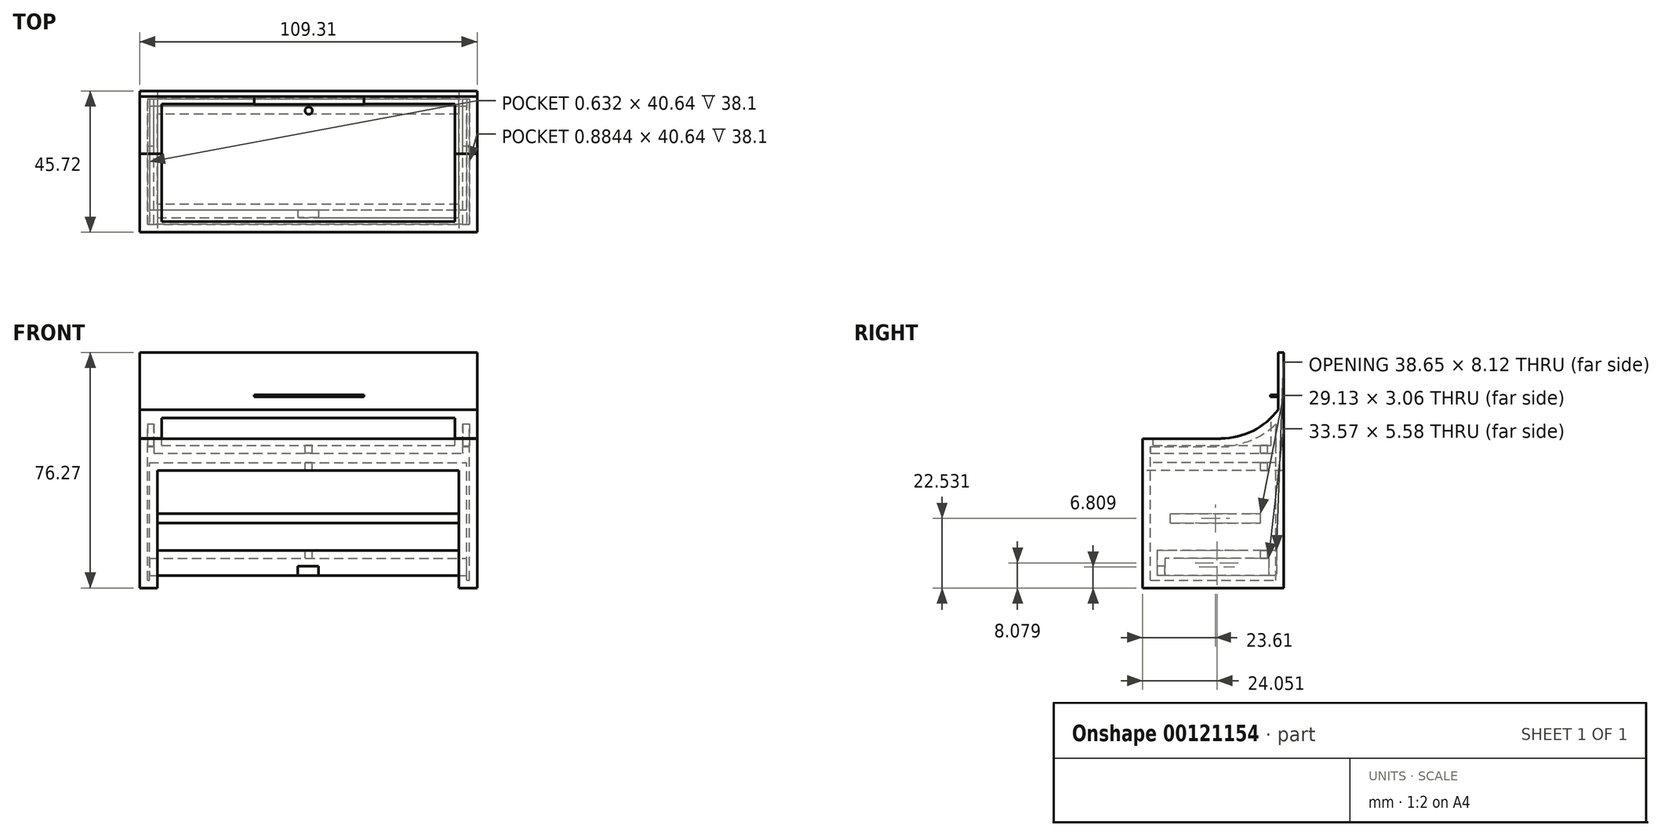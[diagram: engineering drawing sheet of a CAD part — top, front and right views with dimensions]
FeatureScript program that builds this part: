
annotation { "Feature Type Name" : "Feature", "Feature Type Description" : "" }
export const myFeature = defineFeature(function(context is Context, id is Id, definition is map)
    precondition{}
    {
        {
            var Q0;
            Q0=qCreatedBy(makeId("Front.planeOp"),FACE);
            var sketch = newSketch(context, id + "F0", { "sketchPlane" : qUnion([Q0])});
            skLineSegment(sketch, "E0.bottom", {"start": v(-54.76, 0) * mm, "end": v(54.55, 0) * mm});
            skLineSegment(sketch, "E0.top", {"start": v(-54.76, 33.44) * mm, "end": v(54.55, 33.44) * mm});
            skLineSegment(sketch, "E0.left", {"start": v(-54.76, 0) * mm, "end": v(-54.76, 33.44) * mm});
            skLineSegment(sketch, "E0.right", {"start": v(54.55, 0) * mm, "end": v(54.55, 33.44) * mm});
            skSolve(sketch);
        }
        {
            var Q0;
            Q0=makeQuery(id+"F0.imprint","IMPRINT",FACE,{"disambiguationData":[TD([[makeQuery(id+"F0.imprint","IMPRINT",EDGE,{"derivedFrom":sQuery(id+"F0.wireOp",EDGE,"E0.bottom")}),1.0]])]});
            extrude(context, id + "F1", {"entities" : qUnion([Q0]), "depth" : 45.72 * mm});
        }
        {
            var Q0;
            Q0=makeQuery(id+"F1.opExtrude","SWEPT_FACE",FACE,{"disambiguationData":[OSD([sQuery(id+"F0.wireOp",EDGE,"E0.top")])]});
            var sketch = newSketch(context, id + "F2", { "sketchPlane" : qUnion([Q0])});
            skLineSegment(sketch, "E1.bottom", {"start": v(-47.64, -42.28) * mm, "end": v(47.4, -42.28) * mm});
            skLineSegment(sketch, "E1.top", {"start": v(-47.64, -4.14) * mm, "end": v(47.4, -4.14) * mm});
            skLineSegment(sketch, "E1.left", {"start": v(-47.64, -42.28) * mm, "end": v(-47.64, -4.14) * mm});
            skLineSegment(sketch, "E1.right", {"start": v(47.4, -42.28) * mm, "end": v(47.4, -4.14) * mm});
            skSolve(sketch);
        }
        {
            var Q0;
            Q0=makeQuery(id+"F2.imprint","IMPRINT",FACE,{"disambiguationData":[TD([[makeQuery(id+"F2.imprint","IMPRINT",EDGE,{"derivedFrom":sQuery(id+"F2.wireOp",EDGE,"E1.bottom")}),1.0]])]});
            extrude(context, id + "F3", {"entities" : qUnion([Q0]), "operationType" : NewBodyOperationType.REMOVE, "oppositeDirection" : true, "depth" : 25.4 * mm});
        }
        {
            var Q0;
            Q0=makeQuery(id+"F1.opExtrude","CAP_FACE",FACE,{"disambiguationData":[OSD([sQuery(id+"F0.wireOp",EDGE,"E0.bottom"),sQuery(id+"F0.wireOp",EDGE,"E0.top"),sQuery(id+"F0.wireOp",EDGE,"E0.left"),sQuery(id+"F0.wireOp",EDGE,"E0.right")])],"isStart":false});
            var sketch = newSketch(context, id + "F4", { "sketchPlane" : qUnion([Q0])});
            skLineSegment(sketch, "E2.bottom", {"start": v(-54.76, 10.2) * mm, "end": v(54.55, 10.2) * mm});
            skLineSegment(sketch, "E2.top", {"start": v(-54.76, 33.44) * mm, "end": v(54.55, 33.44) * mm});
            skLineSegment(sketch, "E2.left", {"start": v(-54.76, 10.2) * mm, "end": v(-54.76, 33.44) * mm});
            skLineSegment(sketch, "E2.right", {"start": v(54.55, 10.2) * mm, "end": v(54.55, 33.44) * mm});
            skSolve(sketch);
        }
        {
            var Q0;
            Q0=makeQuery(id+"F4.imprint","IMPRINT",FACE,{"disambiguationData":[TD([[makeQuery(id+"F4.imprint","IMPRINT",EDGE,{"derivedFrom":sQuery(id+"F4.wireOp",EDGE,"E2.bottom")}),1.0]])]});
            extrude(context, id + "F5", {"entities" : qUnion([Q0]), "operationType" : NewBodyOperationType.REMOVE, "oppositeDirection" : true, "depth" : 25.4 * mm});
        }
        {
            var Q0;
            Q0=makeQuery(id+"F1.opExtrude","SWEPT_FACE",FACE,{"disambiguationData":[OSD([sQuery(id+"F0.wireOp",EDGE,"E0.right")])]});
            var sketch = newSketch(context, id + "F6", { "sketchPlane" : qUnion([Q0])});
            skCircle(sketch, "E3", {"center": v(-20.32, 33.44) * mm, "radius": 23.08 * mm});
            skSolve(sketch);
        }
        {
            var Q0;
            {var subQ1=sQuery(id+"F0.wireOp",EDGE,"E0.right");var subQ6=makeQuery(id+"F1.opExtrude","SWEPT_EDGE",EDGE,{"disambiguationData":[OSD([sQuery(id+"F0.wireOp",EDGE,"E0.top"),subQ1])]});Q0=makeQuery(id+"F6.imprint","IMPRINT",FACE,{"disambiguationData":[TD([[makeQuery(id+"F6.imprint","IMPRINT",EDGE,{"derivedFrom":subQ6}),1.0]])]});}
            var Q1;
            {var subQ1=sQuery(id+"F0.wireOp",EDGE,"E0.right");var subQ6=makeQuery(id+"F1.opExtrude","SWEPT_EDGE",EDGE,{"disambiguationData":[OSD([sQuery(id+"F0.wireOp",EDGE,"E0.top"),subQ1])]});Q1=makeQuery(id+"F6.imprint","IMPRINT",FACE,{"disambiguationData":[TD([[makeQuery(id+"F6.imprint","IMPRINT",EDGE,{"derivedFrom":subQ6}),-1.0]])]});}
            extrude(context, id + "F7", {"entities" : qUnion([Q0, Q1]), "operationType" : NewBodyOperationType.REMOVE, "oppositeDirection" : true, "depth" : 254 * mm});
        }
        {
            var Q0;
            Q0=makeQuery(id+"F3.boolean.opBoolean","COPY",FACE,{"derivedFrom":makeQuery(id+"F3.opExtrude","CAP_FACE",FACE,{"disambiguationData":[OSD([sQuery(id+"F2.wireOp",EDGE,"E1.bottom"),sQuery(id+"F2.wireOp",EDGE,"E1.top"),sQuery(id+"F2.wireOp",EDGE,"E1.left"),sQuery(id+"F2.wireOp",EDGE,"E1.right")])],"isStart":false})});
            var sketch = newSketch(context, id + "F8", { "sketchPlane" : qUnion([Q0])});
            skCircle(sketch, "E4", {"center": v(0, -6.36) * mm, "radius": 1.17 * mm});
            skSolve(sketch);
        }
        {
            var Q0;
            Q0=makeQuery(id+"F1.opExtrude","SWEPT_FACE",FACE,{"disambiguationData":[OSD([sQuery(id+"F0.wireOp",EDGE,"E0.bottom")])]});
            var sketch = newSketch(context, id + "F9", { "sketchPlane" : qUnion([Q0])});
            skLineSegment(sketch, "E5.bottom", {"start": v(-54.76, 0) * mm, "end": v(-49.05, 0) * mm});
            skLineSegment(sketch, "E5.top", {"start": v(-54.76, 45.72) * mm, "end": v(-49.05, 45.72) * mm});
            skLineSegment(sketch, "E5.left", {"start": v(-54.76, 0) * mm, "end": v(-54.76, 45.72) * mm});
            skLineSegment(sketch, "E5.right", {"start": v(-49.05, 0) * mm, "end": v(-49.05, 45.72) * mm});
            skLineSegment(sketch, "E6.bottom", {"start": v(54.55, 0) * mm, "end": v(48.6, 0) * mm});
            skLineSegment(sketch, "E6.top", {"start": v(54.55, 45.72) * mm, "end": v(48.6, 45.72) * mm});
            skLineSegment(sketch, "E6.left", {"start": v(54.55, 0) * mm, "end": v(54.55, 45.72) * mm});
            skLineSegment(sketch, "E6.right", {"start": v(48.6, 0) * mm, "end": v(48.6, 45.72) * mm});
            skSolve(sketch);
        }
        {
            var Q0;
            Q0=makeQuery(id+"F9.imprint","IMPRINT",FACE,{"disambiguationData":[TD([[makeQuery(id+"F9.imprint","IMPRINT",EDGE,{"derivedFrom":sQuery(id+"F9.wireOp",EDGE,"E6.bottom")}),1.0]])]});
            var Q1;
            Q1=makeQuery(id+"F9.imprint","IMPRINT",FACE,{"disambiguationData":[TD([[makeQuery(id+"F9.imprint","IMPRINT",EDGE,{"derivedFrom":sQuery(id+"F9.wireOp",EDGE,"E5.bottom")}),1.0]])]});
            extrude(context, id + "F10", {"entities" : qUnion([Q0, Q1]), "operationType" : NewBodyOperationType.ADD, "depth" : 38.1 * mm});
        }
        {
            var Q0;
            Q0=makeQuery(id+"F10.opExtrude","SWEPT_FACE",FACE,{"disambiguationData":[OSD([sQuery(id+"F9.wireOp",EDGE,"E5.right")])]});
            var sketch = newSketch(context, id + "F11", { "sketchPlane" : qUnion([Q0])});
            skLineSegment(sketch, "E7.bottom", {"start": v(-36.68, -17.1) * mm, "end": v(-7.55, -17.1) * mm});
            skLineSegment(sketch, "E7.top", {"start": v(-36.68, -14.04) * mm, "end": v(-7.55, -14.04) * mm});
            skLineSegment(sketch, "E7.left", {"start": v(-36.68, -17.1) * mm, "end": v(-36.68, -14.04) * mm});
            skLineSegment(sketch, "E7.right", {"start": v(-7.55, -17.1) * mm, "end": v(-7.55, -14.04) * mm});
            skSolve(sketch);
        }
        {
            var Q0;
            Q0=makeQuery(id+"F11.imprint","IMPRINT",FACE,{"disambiguationData":[TD([[makeQuery(id+"F11.imprint","IMPRINT",EDGE,{"derivedFrom":sQuery(id+"F11.wireOp",EDGE,"E7.bottom")}),1.0]])]});
            extrude(context, id + "F12", {"entities" : qUnion([Q0]), "operationType" : NewBodyOperationType.ADD, "depth" : 101.6 * mm});
        }
        {
            var Q0;
            Q0=makeQuery(id+"F10.boolean.opBoolean","MERGE",FACE,{"derivedFrom":[makeQuery(id+"F1.opExtrude","SWEPT_FACE",FACE,{"disambiguationData":[OSD([sQuery(id+"F0.wireOp",EDGE,"E0.right")])]}),makeQuery(id+"F10.opExtrude","SWEPT_FACE",FACE,{"disambiguationData":[OSD([sQuery(id+"F9.wireOp",EDGE,"E6.left")])]})]});
            var sketch = newSketch(context, id + "F13", { "sketchPlane" : qUnion([Q0])});
            skLineSegment(sketch, "E8", {"start": v(-1.84, 19.62) * mm, "end": v(0, 19.62) * mm});
            skSolve(sketch);
        }
        {
            var Q0;
            {var subQ0=sQuery(id+"F13.wireOp",EDGE,"E8");Q0=makeQuery(id+"F13.imprint","IMPRINT",FACE,{"disambiguationData":[TD([[makeQuery(id+"F13.imprint","IMPRINT",EDGE,{"derivedFrom":subQ0}),1.0]])]});}
            extrude(context, id + "F14", {"entities" : qUnion([Q0]), "operationType" : NewBodyOperationType.REMOVE, "oppositeDirection" : true, "depth" : 127 * mm});
        }
        {
            var Q0;
            Q0=makeQuery(id+"F14.boolean.opBoolean","COPY",FACE,{"derivedFrom":makeQuery(id+"F14.opExtrude","SWEPT_FACE",FACE,{"disambiguationData":[OSD([sQuery(id+"F13.wireOp",EDGE,"E8")])]})});
            extrude(context, id + "F15", {"entities" : qUnion([Q0]), "operationType" : NewBodyOperationType.ADD, "depth" : 18.55 * mm});
        }
        {
            var Q0;
            Q0=makeQuery(id+"F15.opExtrude","SWEPT_FACE",FACE,{"disambiguationData":[OSD([sQuery(id+"F6.wireOp",EDGE,"E3"),sQuery(id+"F13.wireOp",EDGE,"E8")])]});
            var sketch = newSketch(context, id + "F16", { "sketchPlane" : qUnion([Q0])});
            skLineSegment(sketch, "E9.bottom", {"start": v(-17.62, 24.52) * mm, "end": v(17.84, 24.52) * mm});
            skLineSegment(sketch, "E9.top", {"start": v(-17.62, 23.83) * mm, "end": v(17.84, 23.83) * mm});
            skLineSegment(sketch, "E9.left", {"start": v(-17.62, 24.52) * mm, "end": v(-17.62, 23.83) * mm});
            skLineSegment(sketch, "E9.right", {"start": v(17.84, 24.52) * mm, "end": v(17.84, 23.83) * mm});
            skSolve(sketch);
        }
        {
            var Q0;
            Q0=makeQuery(id+"F16.imprint","IMPRINT",FACE,{"disambiguationData":[TD([[makeQuery(id+"F16.imprint","IMPRINT",EDGE,{"derivedFrom":sQuery(id+"F16.wireOp",EDGE,"E9.bottom")}),-1.0]])]});
            extrude(context, id + "F17", {"entities" : qUnion([Q0]), "operationType" : NewBodyOperationType.ADD, "depth" : 2.54 * mm});
        }
        {
            var Q0;
            Q0=makeQuery(id+"F10.opExtrude","SWEPT_FACE",FACE,{"disambiguationData":[OSD([sQuery(id+"F9.wireOp",EDGE,"E6.right")])]});
            var sketch = newSketch(context, id + "F18", { "sketchPlane" : qUnion([Q0])});
            skLineSegment(sketch, "E10.bottom", {"start": v(41, -34.08) * mm, "end": v(2.34, -34.08) * mm});
            skLineSegment(sketch, "E10.top", {"start": v(41, -25.96) * mm, "end": v(2.34, -25.96) * mm});
            skLineSegment(sketch, "E10.left", {"start": v(41, -34.08) * mm, "end": v(41, -25.96) * mm});
            skLineSegment(sketch, "E10.right", {"start": v(2.34, -34.08) * mm, "end": v(2.34, -25.96) * mm});
            skSolve(sketch);
        }
        {
            var Q0;
            Q0=makeQuery(id+"F18.imprint","IMPRINT",FACE,{"disambiguationData":[TD([[makeQuery(id+"F18.imprint","IMPRINT",EDGE,{"derivedFrom":sQuery(id+"F18.wireOp",EDGE,"E10.bottom")}),-1.0]])]});
            extrude(context, id + "F19", {"entities" : qUnion([Q0]), "operationType" : NewBodyOperationType.ADD, "depth" : 99.98 * mm});
        }
        {
            var Q0;
            Q0=makeQuery(id+"F19.opExtrude","SWEPT_FACE",FACE,{"disambiguationData":[OSD([sQuery(id+"F18.wireOp",EDGE,"E10.bottom")])]});
            shell(context, id + "F20", {"entities" : qUnion([Q0]), "thickness" : 2.54 * mm});
        }
        {
            var Q0;
            Q0=makeQuery(id+"F19.opExtrude","SWEPT_FACE",FACE,{"disambiguationData":[OSD([sQuery(id+"F18.wireOp",EDGE,"E10.left")])]});
            var sketch = newSketch(context, id + "F21", { "sketchPlane" : qUnion([Q0])});
            skLineSegment(sketch, "E11.bottom", {"start": v(4.46, -34.08) * mm, "end": v(-4.92, -34.08) * mm});
            skLineSegment(sketch, "E11.top", {"start": v(4.46, -34.08) * mm, "end": v(-4.92, -34.08) * mm});
            skLineSegment(sketch, "E11.left", {"start": v(4.46, -34.08) * mm, "end": v(4.46, -34.08) * mm});
            skLineSegment(sketch, "E11.right", {"start": v(-4.92, -34.08) * mm, "end": v(-4.92, -34.08) * mm});
            skPoint(sketch, "E11.middle", {"position": v(-0.23, -34.08) * mm});
            skLineSegment(sketch, "E12.bottom", {"start": v(3.13, -31.05) * mm, "end": v(-3.59, -31.05) * mm});
            skLineSegment(sketch, "E12.top", {"start": v(3.13, -37.1) * mm, "end": v(-3.59, -37.1) * mm});
            skLineSegment(sketch, "E12.left", {"start": v(3.13, -31.05) * mm, "end": v(3.13, -37.1) * mm});
            skLineSegment(sketch, "E12.right", {"start": v(-3.59, -31.05) * mm, "end": v(-3.59, -37.1) * mm});
            skSolve(sketch);
        }
        {
            var Q0;
            {var subQ5=sQuery(id+"F21.wireOp",EDGE,"E12.bottom");Q0=makeQuery(id+"F21.imprint","IMPRINT",FACE,{"disambiguationData":[TD([[makeQuery(id+"F21.imprint","IMPRINT",EDGE,{"derivedFrom":subQ5}),1.0]])]});}
            extrude(context, id + "F22", {"entities" : qUnion([Q0]), "operationType" : NewBodyOperationType.REMOVE, "oppositeDirection" : true, "depth" : 25.4 * mm});
        }
        {
            var Q0;
            Q0=makeQuery(id+"F8.imprint","IMPRINT",FACE,{"disambiguationData":[TD([[makeQuery(id+"F8.imprint","IMPRINT",EDGE,{"derivedFrom":sQuery(id+"F8.wireOp",EDGE,"E4")}),1.0]])]});
            extrude(context, id + "F23", {"entities" : qUnion([Q0]), "operationType" : NewBodyOperationType.REMOVE, "oppositeDirection" : true, "depth" : 69.4 * mm});
        }
    });
